# Revit family: 1Electronics_Desono_Biamp_Two-Way-Conferencing-Loudspeaker_C-IC6
name_source: partatom
category: Communication Devices
units: mm (PartAtom-declared; Revit-internal decimal feet)

## family parameters
Cut with Voids When Loaded = No
Host = Face
Maintain Annotation Orientation = No
OmniClass Number = 23.85.10.11.14.14.14
Part Type = Normal
Room Calculation Point = No
Round Connector Dimension = Use Diameter
Shared = No

## types (1)
- Default - please load Revit Family Type Catalog
    ABP450 = Yes
    Compliance = ETL listed to comply with UL 1480A and UL 2043;Certifed to CSA C22.2#62368-1;Suitable for use in air handling spaces per NFPA 70, NFPA 90Conforms with City of Chicago Codes
    Connector 450 = 3
    Connector Description = 4-pole Euroblock; 22V 60W 8Ω (240W peak)
    Connector X = 3
    Connector XA = 3
    Continuous Power Handling Nominal Impedance = 22V; 60W @ 8Ω (240W peak)
    Cutout Diameter = 248 mm (9.75)
    Default Elevation = 4' - 0"
    Depth = 0' - 6"
    Description = Desono™ C-IC6 Two-Way 6.5 Ceiling Mount Conferencing Loudspeaker
    Diameter = 0' - 11"
    Grill Material = Biamp - Plastic - Black(Grid)
    Housing Material = Biamp - Plastic - Black
    Input Connection = One 4-pole Euroblock connector for two pair of parallel connections [up to 16AWG];Two RJ-45 connectors
    Manufacturer = Biamp
    Model = C-IC6-B with Amp-450BP
    Mounting Provisions = 4 mounting clamps with 36 mm (1.4) grip range
    Nominal Beamwidth  (H x V) = 130°, conical
    Nominal Maximum SPL @ 1m = Peak - 112dB; Continuous -106dB
    Nominal Sensitivity @ 1m = 1W - 88dB; 2.83V -88dB
    Operating Environment = Indoor in climate-controlled environments
    Operating Mode = Passive with DSP
    Operating Range (-10dB) = 60 Hz to 20 kHz
    Product Documentation Link = https://downloads.biamp.com
    Product Page URL = https://www.biamp.com
    Product data url = https://www.bimobject.com
    Recommended Amplifers = 60W - 120W @ 8Ω (22V - 31V); Tesira AMP-450BP
    Shipping Weight = 24.03 lb
    TCM-X = Yes
    TCM-XA = Yes
    Transducers = LF 1 x 6.5 (165 mm) treated paper cone; HF 1 x 1 (25 mm) soft dome
    URL = https://www.biamp.com
    Weight = 7.72 lb
    connector = No

## geometry (parser evidence)
native form markers: Sweep x6
no freeform markers — native parametric forms only
